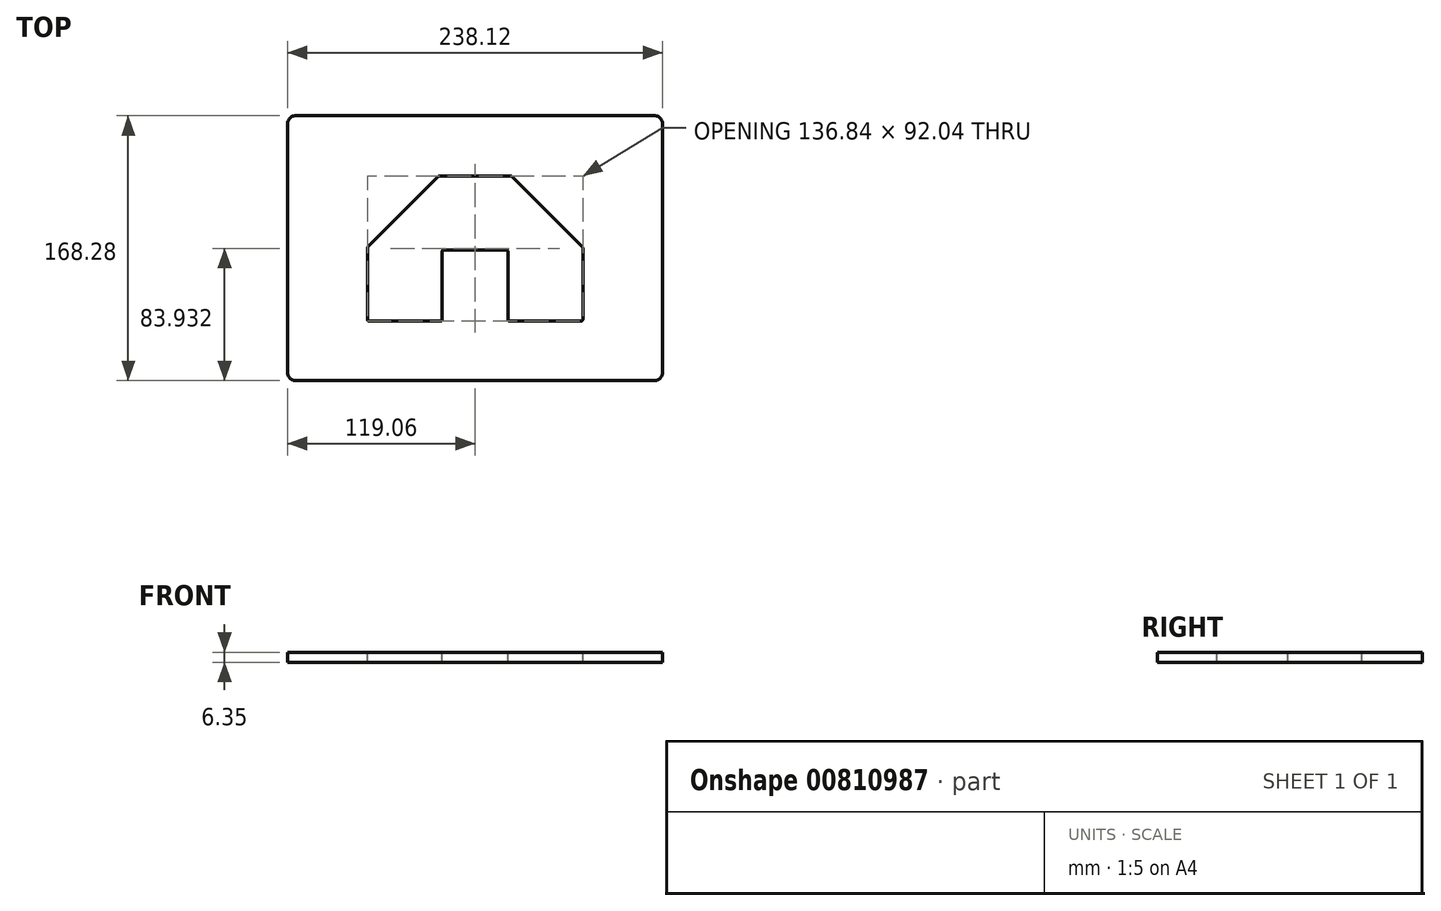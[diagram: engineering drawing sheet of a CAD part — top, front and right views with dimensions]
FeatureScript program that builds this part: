
annotation { "Feature Type Name" : "Feature", "Feature Type Description" : "" }
export const myFeature = defineFeature(function(context is Context, id is Id, definition is map)
    precondition{}
    {
        {
            var Q0;
            Q0=qCreatedBy(makeId("Top.planeOp"),FACE);
            var sketch = newSketch(context, id + "F0", { "sketchPlane" : qUnion([Q0])});
            skLineSegment(sketch, "E0.bottom", {"start": v(-113.98, 84.14) * mm, "end": v(113.98, 84.14) * mm});
            skLineSegment(sketch, "E0.top", {"start": v(-113.98, -84.14) * mm, "end": v(113.98, -84.14) * mm});
            skLineSegment(sketch, "E0.left", {"start": v(-119.06, 79.06) * mm, "end": v(-119.06, -79.06) * mm});
            skLineSegment(sketch, "E0.right", {"start": v(119.06, 79.06) * mm, "end": v(119.06, -79.06) * mm});
            skPoint(sketch, "E0.middle", {"position": v(0, 0) * mm});
            skPoint(sketch, "E1.visualSharp", {"position": v(-119.06, -84.14) * mm});
            skArc(sketch, "E1.filletArc", {"start": v(-119.06, -79.06) * mm, "mid": v(-117.57, -82.65) * mm, "end": v(-113.98, -84.14) * mm});
            skPoint(sketch, "E2.visualSharp", {"position": v(119.06, -84.14) * mm});
            skArc(sketch, "E2.filletArc", {"start": v(113.98, -84.14) * mm, "mid": v(117.57, -82.65) * mm, "end": v(119.06, -79.06) * mm});
            skPoint(sketch, "E3.visualSharp", {"position": v(119.06, 84.14) * mm});
            skArc(sketch, "E3.filletArc", {"start": v(119.06, 79.06) * mm, "mid": v(117.57, 82.65) * mm, "end": v(113.98, 84.14) * mm});
            skPoint(sketch, "E4.visualSharp", {"position": v(-119.06, 84.14) * mm});
            skArc(sketch, "E4.filletArc", {"start": v(-113.98, 84.14) * mm, "mid": v(-117.57, 82.65) * mm, "end": v(-119.06, 79.06) * mm});
            skSolve(sketch);
        }
        {
            var Q0;
            Q0 = qSketchRegion(id + "F0", true);
            extrude(context, id + "F1", {"entities" : qUnion([Q0]), "depth" : 6.35 * mm, "offsetDistance" : 25.4 * mm});
        }
        {
            var Q0;
            Q0=makeQuery(id+"F1.opExtrude","CAP_FACE",FACE,{"disambiguationData":[OSD([sQuery(id+"F0.wireOp",EDGE,"E0.bottom"),sQuery(id+"F0.wireOp",EDGE,"E0.top"),sQuery(id+"F0.wireOp",EDGE,"E0.left"),sQuery(id+"F0.wireOp",EDGE,"E0.right"),sQuery(id+"F0.wireOp",EDGE,"E1.filletArc"),sQuery(id+"F0.wireOp",EDGE,"E2.filletArc"),sQuery(id+"F0.wireOp",EDGE,"E3.filletArc"),sQuery(id+"F0.wireOp",EDGE,"E4.filletArc")])],"isStart":false});
            var sketch = newSketch(context, id + "F2", { "sketchPlane" : qUnion([Q0])});
            skLineSegment(sketch, "E5", {"start": v(0, 44.54) * mm, "end": v(-22.6, 44.54) * mm});
            skLineSegment(sketch, "E6", {"start": v(-22.6, 44.54) * mm, "end": v(-67.15, 0) * mm});
            skLineSegment(sketch, "E7", {"start": v(-67.15, 0) * mm, "end": v(-67.15, -44.96) * mm});
            skLineSegment(sketch, "E8", {"start": v(-67.15, -44.96) * mm, "end": v(-22.2, -44.96) * mm});
            skLineSegment(sketch, "E9", {"start": v(-22.2, -44.96) * mm, "end": v(-22.2, 0) * mm});
            skLineSegment(sketch, "E10", {"start": v(-22.2, 0) * mm, "end": v(0, 0) * mm});
            skLineSegment(sketch, "E11.MirrorCS", {"start": v(0, 44.54) * mm, "end": v(22.6, 44.54) * mm});
            skLineSegment(sketch, "E12.MirrorCS", {"start": v(22.6, 44.54) * mm, "end": v(67.15, 0) * mm});
            skLineSegment(sketch, "E13.MirrorCS", {"start": v(67.15, 0) * mm, "end": v(67.15, -44.96) * mm});
            skLineSegment(sketch, "E14.MirrorCS", {"start": v(67.15, -44.96) * mm, "end": v(22.2, -44.96) * mm});
            skLineSegment(sketch, "E15.MirrorCS", {"start": v(22.2, -44.96) * mm, "end": v(22.2, 0) * mm});
            skLineSegment(sketch, "E16.MirrorCS", {"start": v(22.2, 0) * mm, "end": v(0, 0) * mm});
            skSolve(sketch);
        }
        {
            var Q0;
            Q0 = qSketchRegion(id + "F2", true);
            extrude(context, id + "F3", {"entities" : qUnion([Q0]), "operationType" : NewBodyOperationType.REMOVE, "oppositeDirection" : true, "depth" : 25.4 * mm, "offsetDistance" : 25.4 * mm});
        }
        {
            var Q0;
            Q0=makeQuery(id+"F1.opExtrude","CAP_FACE",FACE,{"disambiguationData":[OSD([sQuery(id+"F0.wireOp",EDGE,"E0.bottom"),sQuery(id+"F0.wireOp",EDGE,"E0.top"),sQuery(id+"F0.wireOp",EDGE,"E0.left"),sQuery(id+"F0.wireOp",EDGE,"E0.right"),sQuery(id+"F0.wireOp",EDGE,"E1.filletArc"),sQuery(id+"F0.wireOp",EDGE,"E2.filletArc"),sQuery(id+"F0.wireOp",EDGE,"E3.filletArc"),sQuery(id+"F0.wireOp",EDGE,"E4.filletArc")])],"isStart":false});
            var sketch = newSketch(context, id + "F4", { "sketchPlane" : qUnion([Q0])});
            skLineSegment(sketch, "E17.0", {"start": v(-23.36, 45.58) * mm, "end": v(-68.19, 0.76) * mm});
            skLineSegment(sketch, "E17.1", {"start": v(-68.42, 0.2) * mm, "end": v(-68.42, -45.44) * mm});
            skLineSegment(sketch, "E17.2", {"start": v(-22.8, 45.81) * mm, "end": v(22.8, 45.81) * mm});
            skLineSegment(sketch, "E17.3", {"start": v(-67.63, -46.23) * mm, "end": v(-21.7, -46.23) * mm});
            skLineSegment(sketch, "E17.4", {"start": v(-20.92, -45.44) * mm, "end": v(-20.92, -2.06) * mm});
            skLineSegment(sketch, "E17.5", {"start": v(20.13, -1.27) * mm, "end": v(-20.13, -1.27) * mm});
            skLineSegment(sketch, "E17.6", {"start": v(23.36, 45.58) * mm, "end": v(68.19, 0.76) * mm});
            skLineSegment(sketch, "E17.7", {"start": v(68.42, 0.2) * mm, "end": v(68.42, -45.44) * mm});
            skLineSegment(sketch, "E17.8", {"start": v(67.63, -46.23) * mm, "end": v(21.7, -46.23) * mm});
            skLineSegment(sketch, "E17.9", {"start": v(20.92, -45.44) * mm, "end": v(20.92, -2.06) * mm});
            skPoint(sketch, "E18.visualSharp", {"position": v(-23.13, 45.81) * mm});
            skArc(sketch, "E18.filletArc", {"start": v(-22.8, 45.81) * mm, "mid": v(-23.1, 45.75) * mm, "end": v(-23.36, 45.58) * mm});
            skPoint(sketch, "E19.visualSharp", {"position": v(23.13, 45.81) * mm});
            skArc(sketch, "E19.filletArc", {"start": v(23.36, 45.58) * mm, "mid": v(23.1, 45.75) * mm, "end": v(22.8, 45.81) * mm});
            skPoint(sketch, "E20.visualSharp", {"position": v(68.42, 0.53) * mm});
            skArc(sketch, "E20.filletArc", {"start": v(68.42, 0.2) * mm, "mid": v(68.36, 0.5) * mm, "end": v(68.19, 0.76) * mm});
            skPoint(sketch, "E21.visualSharp", {"position": v(68.42, -46.23) * mm});
            skArc(sketch, "E21.filletArc", {"start": v(67.63, -46.23) * mm, "mid": v(68.19, -46) * mm, "end": v(68.42, -45.44) * mm});
            skPoint(sketch, "E22.visualSharp", {"position": v(20.92, -46.23) * mm});
            skArc(sketch, "E22.filletArc", {"start": v(20.92, -45.44) * mm, "mid": v(21.15, -46) * mm, "end": v(21.7, -46.23) * mm});
            skPoint(sketch, "E23.visualSharp", {"position": v(20.92, -1.27) * mm});
            skArc(sketch, "E23.filletArc", {"start": v(20.92, -2.06) * mm, "mid": v(20.69, -1.5) * mm, "end": v(20.13, -1.27) * mm});
            skPoint(sketch, "E24.visualSharp", {"position": v(-20.92, -1.27) * mm});
            skArc(sketch, "E24.filletArc", {"start": v(-20.13, -1.27) * mm, "mid": v(-20.69, -1.5) * mm, "end": v(-20.92, -2.06) * mm});
            skPoint(sketch, "E25.visualSharp", {"position": v(-20.92, -46.23) * mm});
            skArc(sketch, "E25.filletArc", {"start": v(-21.7, -46.23) * mm, "mid": v(-21.15, -46) * mm, "end": v(-20.92, -45.44) * mm});
            skPoint(sketch, "E26.visualSharp", {"position": v(-68.42, -46.23) * mm});
            skArc(sketch, "E26.filletArc", {"start": v(-68.42, -45.44) * mm, "mid": v(-68.19, -46) * mm, "end": v(-67.63, -46.23) * mm});
            skPoint(sketch, "E27.visualSharp", {"position": v(-68.42, 0.53) * mm});
            skArc(sketch, "E27.filletArc", {"start": v(-68.19, 0.76) * mm, "mid": v(-68.36, 0.5) * mm, "end": v(-68.42, 0.2) * mm});
            skSolve(sketch);
        }
        {
            var Q0;
            Q0 = qSketchRegion(id + "F4", true);
            extrude(context, id + "F5", {"entities" : qUnion([Q0]), "operationType" : NewBodyOperationType.REMOVE, "oppositeDirection" : true, "depth" : 25.4 * mm, "offsetDistance" : 25.4 * mm});
        }
    });
